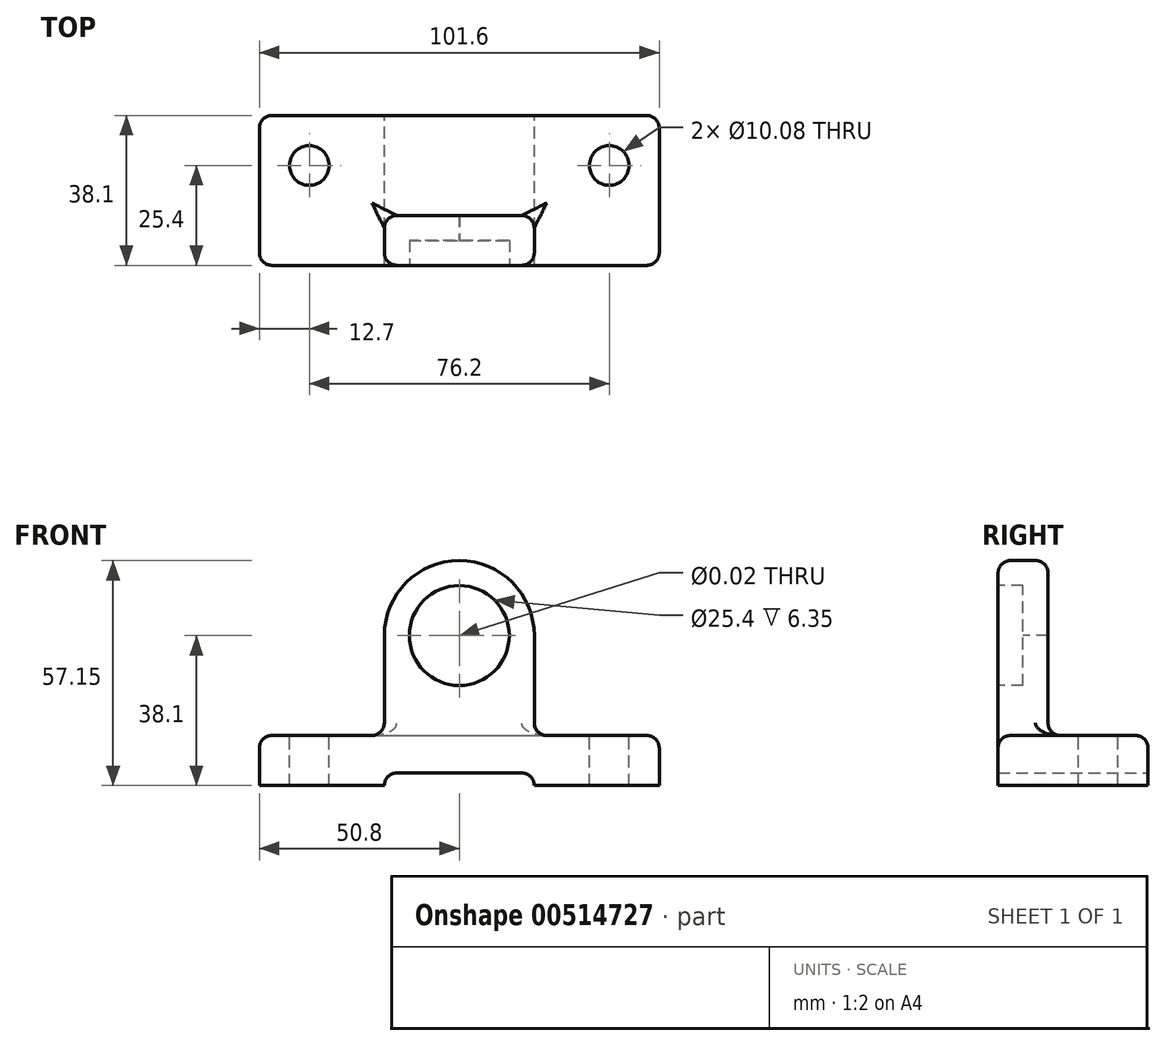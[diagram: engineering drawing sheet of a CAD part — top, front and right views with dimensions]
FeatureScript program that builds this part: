
annotation { "Feature Type Name" : "Feature", "Feature Type Description" : "" }
export const myFeature = defineFeature(function(context is Context, id is Id, definition is map)
    precondition{}
    {
        {
            var Q0;
            Q0=qCreatedBy(makeId("Top.planeOp"),FACE);
            var sketch = newSketch(context, id + "F0", { "sketchPlane" : qUnion([Q0])});
            skLineSegment(sketch, "E0.bottom", {"start": v(0, 0) * mm, "end": v(101.6, 0) * mm});
            skLineSegment(sketch, "E0.top", {"start": v(0, 38.1) * mm, "end": v(101.6, 38.1) * mm});
            skLineSegment(sketch, "E0.left", {"start": v(0, 0) * mm, "end": v(0, 38.1) * mm});
            skLineSegment(sketch, "E0.right", {"start": v(101.6, 0) * mm, "end": v(101.6, 38.1) * mm});
            skSolve(sketch);
        }
        {
            var Q0;
            Q0=makeQuery(id+"F0.imprint","IMPRINT",FACE,{"disambiguationData":[TD([[makeQuery(id+"F0.imprint","IMPRINT",EDGE,{"derivedFrom":sQuery(id+"F0.wireOp",EDGE,"E0.bottom")}),1.0]])]});
            extrude(context, id + "F1", {"entities" : qUnion([Q0]), "depth" : 12.7 * mm, "offsetDistance" : 25.4 * mm});
        }
        {
            var Q0;
            Q0=makeQuery(id+"F1.opExtrude","SWEPT_FACE",FACE,{"disambiguationData":[OSD([sQuery(id+"F0.wireOp",EDGE,"E0.bottom")])]});
            var sketch = newSketch(context, id + "F2", { "sketchPlane" : qUnion([Q0])});
            skLineSegment(sketch, "E1", {"start": v(31.75, 0) * mm, "end": v(31.75, 38.1) * mm});
            skLineSegment(sketch, "E2", {"start": v(12.82, 38.1) * mm, "end": v(69.85, 38.1) * mm, "construction": true});
            skArc(sketch, "E3", {"start": v(31.75, 38.1) * mm, "mid": v(50.8, 57.15) * mm, "end": v(69.85, 38.1) * mm});
            skLineSegment(sketch, "E4", {"start": v(69.85, 38.1) * mm, "end": v(69.85, 0) * mm});
            skLineSegment(sketch, "E5", {"start": v(31.75, 0) * mm, "end": v(69.85, 0) * mm});
            skLineSegment(sketch, "E6", {"start": v(50.8, 71.63) * mm, "end": v(50.8, -8.08) * mm, "construction": true});
            skPoint(sketch, "E6.startSnap0", {"position": v(50.8, 0) * mm});
            skSolve(sketch);
        }
        {
            var Q0;
            Q0 = qSketchRegion(id + "F2", true);
            extrude(context, id + "F3", {"entities" : qUnion([Q0]), "operationType" : NewBodyOperationType.ADD, "oppositeDirection" : true, "depth" : 12.7 * mm, "offsetDistance" : 25.4 * mm});
        }
        {
            var Q0;
            Q0=sQuery(id+"F2.wireOp",VERTEX,"E3.center");
            var Q1;
            Q1=makeQuery(id+"F1.opExtrude","SWEPT_BODY",BODY,{"disambiguationData":[OSD([sQuery(id+"F0.wireOp",EDGE,"E0.bottom"),sQuery(id+"F0.wireOp",EDGE,"E0.top"),sQuery(id+"F0.wireOp",EDGE,"E0.left"),sQuery(id+"F0.wireOp",EDGE,"E0.right")])]});
            hole(context, id + "F4", {"style" : HoleStyle.C_BORE, "endStyle" : HoleEndStyle.THROUGH, "standardTappedOrClearance" : lookupTablePath({ "standard" : "ANSI", "size" : "15/32 (0.47)", "type" : "Drilled" }), "standardBlindInLast" : lookupTablePath({ "standard" : "ANSI", "size" : "15/32", "type" : "Drilled" }), "holeDiameter" : 15 / 812.8 * mm, "cBoreDiameter" : 25.4 * mm, "cBoreDepth" : 6.35 * mm, "isTappedThrough" : true, "tappedDepth" : 12.7 * mm, "tapClearance" : 3, "locations" : qUnion([Q0]), "scope" : qUnion([Q1])});
        }
        {
            var Q0;
            Q0=makeQuery(id+"F1.opExtrude","SWEPT_FACE",FACE,{"disambiguationData":[OSD([sQuery(id+"F0.wireOp",EDGE,"E0.top")])]});
            var sketch = newSketch(context, id + "F5", { "sketchPlane" : qUnion([Q0])});
            skLineSegment(sketch, "E7", {"start": v(-69.85, 0) * mm, "end": v(-69.85, 3.17) * mm});
            skLineSegment(sketch, "E8", {"start": v(-69.85, 3.17) * mm, "end": v(-31.75, 3.18) * mm});
            skLineSegment(sketch, "E9", {"start": v(-31.75, 3.18) * mm, "end": v(-31.75, 0) * mm});
            skLineSegment(sketch, "E10", {"start": v(-31.75, 0) * mm, "end": v(-69.85, 0) * mm});
            skSolve(sketch);
        }
        {
            var Q0;
            Q0 = qSketchRegion(id + "F5", true);
            extrude(context, id + "F6", {"entities" : qUnion([Q0]), "operationType" : NewBodyOperationType.REMOVE, "endBound" : BoundingType.THROUGH_ALL, "oppositeDirection" : true, "depth" : 25.4 * mm, "offsetDistance" : 25.4 * mm});
        }
        {
            var Q0;
            Q0=makeQuery(id+"F1.opExtrude","CAP_FACE",FACE,{"disambiguationData":[OSD([sQuery(id+"F0.wireOp",EDGE,"E0.bottom"),sQuery(id+"F0.wireOp",EDGE,"E0.top"),sQuery(id+"F0.wireOp",EDGE,"E0.left"),sQuery(id+"F0.wireOp",EDGE,"E0.right")])],"isStart":false});
            var sketch = newSketch(context, id + "F7", { "sketchPlane" : qUnion([Q0])});
            skCircle(sketch, "E11", {"center": v(12.7, 25.4) * mm, "radius": 6.35 * mm});
            skCircle(sketch, "E12", {"center": v(88.9, 25.4) * mm, "radius": 6.35 * mm});
            skSolve(sketch);
        }
        {
            var Q0;
            Q0=sQuery(id+"F7.wireOp",VERTEX,"E11.center");
            var Q1;
            Q1=makeQuery(id+"F1.opExtrude","SWEPT_BODY",BODY,{"disambiguationData":[OSD([sQuery(id+"F0.wireOp",EDGE,"E0.bottom"),sQuery(id+"F0.wireOp",EDGE,"E0.top"),sQuery(id+"F0.wireOp",EDGE,"E0.left"),sQuery(id+"F0.wireOp",EDGE,"E0.right")])]});
            hole(context, id + "F8", {"style" : HoleStyle.SIMPLE, "endStyle" : HoleEndStyle.THROUGH, "standardTappedOrClearance" : lookupTablePath({ "standard" : "ANSI", "fit" : "Normal (ASME)", "size" : "3/8", "type" : "Clearance" }), "standardBlindInLast" : lookupTablePath({ "fit" : "Free", "standard" : "ANSI", "size" : "3/8", "type" : "Clearance" }), "holeDiameter" : 10.08 * mm, "isTappedThrough" : true, "tappedDepth" : 12.7 * mm, "tapClearance" : 3, "locations" : qUnion([Q0]), "scope" : qUnion([Q1])});
        }
        {
            var Q0;
            Q0=sQuery(id+"F7.wireOp",VERTEX,"E12.center");
            var Q1;
            Q1=makeQuery(id+"F1.opExtrude","SWEPT_BODY",BODY,{"disambiguationData":[OSD([sQuery(id+"F0.wireOp",EDGE,"E0.bottom"),sQuery(id+"F0.wireOp",EDGE,"E0.top"),sQuery(id+"F0.wireOp",EDGE,"E0.left"),sQuery(id+"F0.wireOp",EDGE,"E0.right")])]});
            hole(context, id + "F9", {"style" : HoleStyle.SIMPLE, "endStyle" : HoleEndStyle.THROUGH, "standardTappedOrClearance" : lookupTablePath({ "standard" : "ANSI", "fit" : "Normal (ASME)", "size" : "3/8", "type" : "Clearance" }), "standardBlindInLast" : lookupTablePath({ "fit" : "Free", "standard" : "ANSI", "size" : "3/8", "type" : "Clearance" }), "holeDiameter" : 10.08 * mm, "isTappedThrough" : true, "tappedDepth" : 12.7 * mm, "tapClearance" : 3, "locations" : qUnion([Q0]), "scope" : qUnion([Q1])});
        }
        {
            var Q0;
            Q0=makeQuery(id+"F1.opExtrude","SWEPT_EDGE",EDGE,{"disambiguationData":[OSD([sQuery(id+"F0.wireOp",EDGE,"E0.bottom"),sQuery(id+"F0.wireOp",EDGE,"E0.right")])]});
            var Q1;
            Q1=makeQuery(id+"F1.opExtrude","SWEPT_EDGE",EDGE,{"disambiguationData":[OSD([sQuery(id+"F0.wireOp",EDGE,"E0.top"),sQuery(id+"F0.wireOp",EDGE,"E0.right")])]});
            var Q2;
            Q2=makeQuery(id+"F1.opExtrude","SWEPT_EDGE",EDGE,{"disambiguationData":[OSD([sQuery(id+"F0.wireOp",EDGE,"E0.bottom"),sQuery(id+"F0.wireOp",EDGE,"E0.left")])]});
            var Q3;
            Q3=makeQuery(id+"F1.opExtrude","SWEPT_EDGE",EDGE,{"disambiguationData":[OSD([sQuery(id+"F0.wireOp",EDGE,"E0.top"),sQuery(id+"F0.wireOp",EDGE,"E0.left")])]});
            fillet(context, id + "F10", {"entities" : qUnion([Q0, Q1, Q2, Q3]), "radius" : 3.17 * mm, "tangentPropagation" : true, "allowEdgeOverflow" : false});
        }
        {
            var Q0;
            Q0=makeQuery(id+"F6.boolean.opBoolean","COPY",EDGE,{"derivedFrom":makeQuery(id+"F6.opExtrude","SWEPT_EDGE",EDGE,{"disambiguationData":[OSD([sQuery(id+"F5.wireOp",EDGE,"E8"),sQuery(id+"F5.wireOp",EDGE,"E9")])]})});
            var Q1;
            Q1=makeQuery(id+"F6.boolean.opBoolean","COPY",EDGE,{"derivedFrom":makeQuery(id+"F6.opExtrude","SWEPT_EDGE",EDGE,{"disambiguationData":[OSD([sQuery(id+"F5.wireOp",EDGE,"E7"),sQuery(id+"F5.wireOp",EDGE,"E8")])]})});
            fillet(context, id + "F11", {"entities" : qUnion([Q0, Q1]), "radius" : 3.17 * mm, "tangentPropagation" : true, "allowEdgeOverflow" : false});
        }
        {
            var Q0;
            Q0=makeQuery(id+"F3.boolean.opBoolean","INTERSECT",EDGE,{"derivedFrom":[makeQuery(id+"F1.opExtrude","CAP_FACE",FACE,{"disambiguationData":[OSD([sQuery(id+"F0.wireOp",EDGE,"E0.bottom"),sQuery(id+"F0.wireOp",EDGE,"E0.top"),sQuery(id+"F0.wireOp",EDGE,"E0.left"),sQuery(id+"F0.wireOp",EDGE,"E0.right")])],"isStart":false}),makeQuery(id+"F3.opExtrude","SWEPT_FACE",FACE,{"disambiguationData":[OSD([sQuery(id+"F2.wireOp",EDGE,"E4")])]})]});
            var Q1;
            Q1=makeQuery(id+"F3.boolean.opBoolean","INTERSECT",EDGE,{"derivedFrom":[makeQuery(id+"F1.opExtrude","CAP_FACE",FACE,{"disambiguationData":[OSD([sQuery(id+"F0.wireOp",EDGE,"E0.bottom"),sQuery(id+"F0.wireOp",EDGE,"E0.top"),sQuery(id+"F0.wireOp",EDGE,"E0.left"),sQuery(id+"F0.wireOp",EDGE,"E0.right")])],"isStart":false}),makeQuery(id+"F3.opExtrude","CAP_FACE",FACE,{"disambiguationData":[OSD([sQuery(id+"F2.wireOp",EDGE,"E1"),sQuery(id+"F2.wireOp",EDGE,"E3"),sQuery(id+"F2.wireOp",EDGE,"E4"),sQuery(id+"F2.wireOp",EDGE,"E5")])],"isStart":false})]});
            var Q2;
            Q2=makeQuery(id+"F3.boolean.opBoolean","INTERSECT",EDGE,{"derivedFrom":[makeQuery(id+"F1.opExtrude","CAP_FACE",FACE,{"disambiguationData":[OSD([sQuery(id+"F0.wireOp",EDGE,"E0.bottom"),sQuery(id+"F0.wireOp",EDGE,"E0.top"),sQuery(id+"F0.wireOp",EDGE,"E0.left"),sQuery(id+"F0.wireOp",EDGE,"E0.right")])],"isStart":false}),makeQuery(id+"F3.opExtrude","SWEPT_FACE",FACE,{"disambiguationData":[OSD([sQuery(id+"F2.wireOp",EDGE,"E1")])]})]});
            fillet(context, id + "F12", {"entities" : qUnion([Q0, Q1, Q2]), "radius" : 3.17 * mm, "tangentPropagation" : true, "allowEdgeOverflow" : false});
        }
        {
            var Q0;
            Q0=makeQuery(id+"F3.opExtrude","SWEPT_FACE",FACE,{"disambiguationData":[OSD([sQuery(id+"F2.wireOp",EDGE,"E4")])]});
            var Q1;
            Q1=makeQuery(id+"F3.opExtrude","SWEPT_FACE",FACE,{"disambiguationData":[OSD([sQuery(id+"F2.wireOp",EDGE,"E3")])]});
            var Q2;
            Q2=makeQuery(id+"F3.opExtrude","SWEPT_FACE",FACE,{"disambiguationData":[OSD([sQuery(id+"F2.wireOp",EDGE,"E1")])]});
            fillet(context, id + "F13", {"entities" : qUnion([Q0, Q1, Q2]), "radius" : 3.17 * mm, "tangentPropagation" : true, "allowEdgeOverflow" : false});
        }
    });
